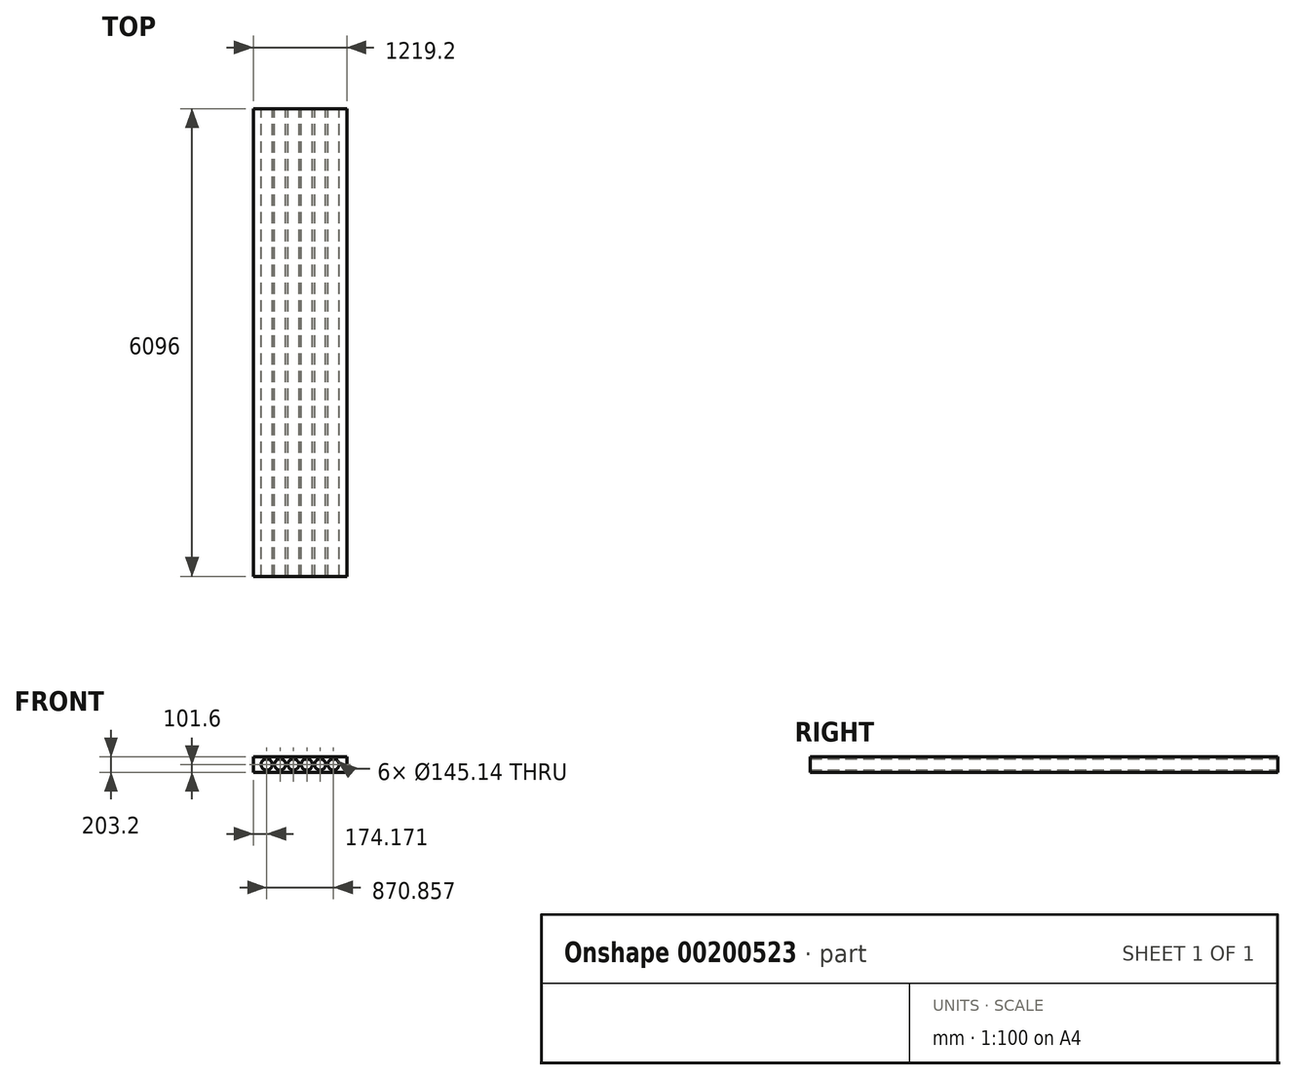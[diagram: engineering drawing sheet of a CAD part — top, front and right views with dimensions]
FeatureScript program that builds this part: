
annotation { "Feature Type Name" : "Feature", "Feature Type Description" : "" }
export const myFeature = defineFeature(function(context is Context, id is Id, definition is map)
    precondition{}
    {
        {
            assignVariable(context, id + "F0", {"name" : "PlankLength", "anyValue" : 6096 * mm});
        }
        {
            var Q0;
            Q0=qCreatedBy(makeId("Front.planeOp"),FACE);
            var sketch = newSketch(context, id + "F1", { "sketchPlane" : qUnion([Q0])});
            skLineSegment(sketch, "E0.bottom", {"start": v(-609.6, 0) * mm, "end": v(609.6, 0) * mm});
            skLineSegment(sketch, "E0.top", {"start": v(-609.6, 203.2) * mm, "end": v(609.6, 203.2) * mm});
            skLineSegment(sketch, "E0.left", {"start": v(-609.6, 0) * mm, "end": v(-609.6, 203.2) * mm});
            skLineSegment(sketch, "E0.right", {"start": v(609.6, 0) * mm, "end": v(609.6, 203.2) * mm});
            skLineSegment(sketch, "E1", {"start": v(-609.6, 101.6) * mm, "end": v(609.6, 101.6) * mm, "construction": true});
            skCircle(sketch, "E2", {"center": v(-435.43, 101.6) * mm, "radius": 72.57 * mm});
            skCircle(sketch, "E3.1.0.0", {"center": v(-261.26, 101.6) * mm, "radius": 72.57 * mm});
            skCircle(sketch, "E3.2.0.0", {"center": v(-87.09, 101.6) * mm, "radius": 72.57 * mm});
            skCircle(sketch, "E3.3.0.0", {"center": v(87.09, 101.6) * mm, "radius": 72.57 * mm});
            skCircle(sketch, "E3.4.0.0", {"center": v(261.26, 101.6) * mm, "radius": 72.57 * mm});
            skCircle(sketch, "E3.5.0.0", {"center": v(435.43, 101.6) * mm, "radius": 72.57 * mm});
            skLineSegment(sketch, "E3.direction1", {"start": v(-435.43, 101.6) * mm, "end": v(-261.26, 101.6) * mm, "construction": true});
            skSolve(sketch);
        }
        {
            var Q0;
            Q0=qSketchRegion(id+"F1",true);
            extrude(context, id + "F2", {"entities" : qUnion([Q0]), "depth" : getVariable(context, 'PlankLength'), "offsetDistance" : 25.4 * mm});
        }
    });
